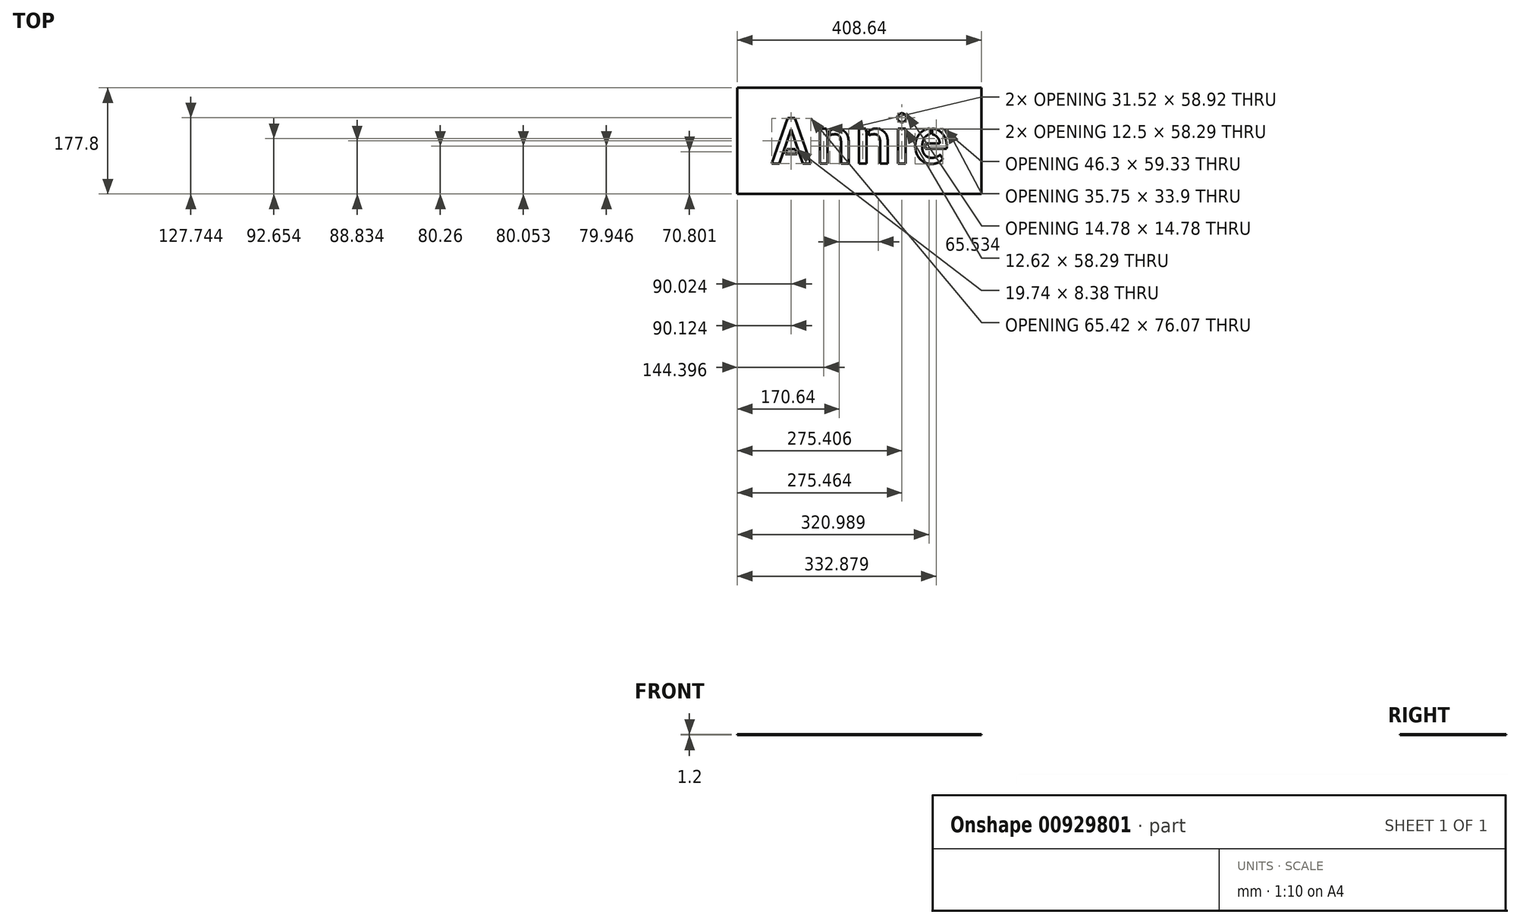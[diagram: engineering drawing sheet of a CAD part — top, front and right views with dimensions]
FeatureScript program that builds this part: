
annotation { "Feature Type Name" : "Feature", "Feature Type Description" : "" }
export const myFeature = defineFeature(function(context is Context, id is Id, definition is map)
    precondition{}
    {
        {
            var Q0;
            Q0=qCreatedBy(makeId("Top.planeOp"),FACE);
            var sketch = newSketch(context, id + "F0", { "sketchPlane" : qUnion([Q0])});
            skPoint(sketch, "E0.middle", {"position": v(0, 0) * mm});
            skText(sketch, "E1", { "text": "Annie\n", "fontName": "AllertaStencil-Regular.ttf"});
            skLineSegment(sketch, "E2.bottom", {"start": v(-204.32, 88.9) * mm, "end": v(204.32, 88.9) * mm});
            skLineSegment(sketch, "E2.top", {"start": v(-204.32, -88.9) * mm, "end": v(204.32, -88.9) * mm});
            skLineSegment(sketch, "E2.left", {"start": v(-204.32, 88.9) * mm, "end": v(-204.32, -88.9) * mm});
            skLineSegment(sketch, "E2.right", {"start": v(204.32, 88.9) * mm, "end": v(204.32, -88.9) * mm});
            const initialGuessF0  = {"E1": [-0.15352, -0.0381, 1, 0, 0.0762]};
            skSetInitialGuess(sketch, initialGuessF0);
            skSolve(sketch);
        }
        {
            var Q0;
            Q0=makeQuery(id+"F0.imprint","IMPRINT",FACE,{"disambiguationData":[TD([[makeQuery(id+"F0.imprint","IMPRINT",EDGE,{"derivedFrom":sQuery(id+"F0.wireOp",EDGE,"E1.sketch_text.stroke-0")}),1.0]])]});
            var Q1;
            Q1=makeQuery(id+"F0.imprint","IMPRINT",FACE,{"disambiguationData":[TD([[makeQuery(id+"F0.imprint","IMPRINT",EDGE,{"derivedFrom":sQuery(id+"F0.wireOp",EDGE,"E1.sketch_text.stroke-8")}),1.0]])]});
            var Q2;
            Q2=makeQuery(id+"F0.imprint","IMPRINT",FACE,{"disambiguationData":[TD([[makeQuery(id+"F0.imprint","IMPRINT",EDGE,{"derivedFrom":sQuery(id+"F0.wireOp",EDGE,"E1.sketch_text.stroke-73")}),1.0]])]});
            extrude(context, id + "F1", {"entities" : qUnion([Q0, Q1, Q2]), "depth" : 1.2 * mm, "offsetDistance" : 25.4 * mm});
        }
    });
